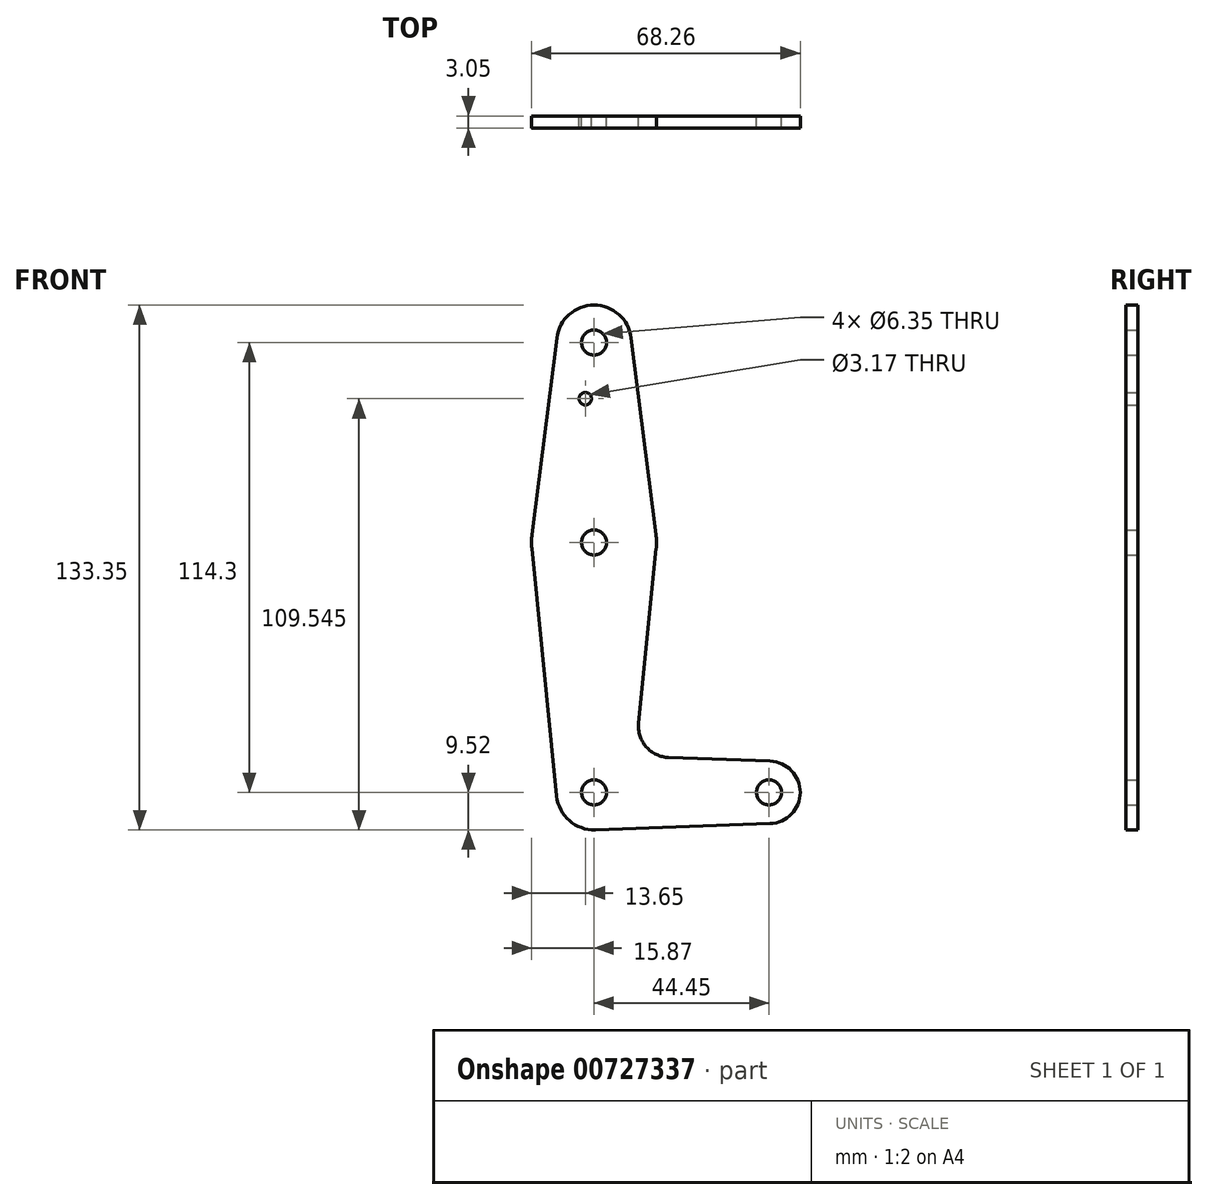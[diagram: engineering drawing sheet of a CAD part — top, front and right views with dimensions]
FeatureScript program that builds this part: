
annotation { "Feature Type Name" : "Feature", "Feature Type Description" : "" }
export const myFeature = defineFeature(function(context is Context, id is Id, definition is map)
    precondition{}
    {
        {
            var Q0;
            Q0=qCreatedBy(makeId("Front.planeOp"),FACE);
            var sketch = newSketch(context, id + "F0", { "sketchPlane" : qUnion([Q0])});
            skLineSegment(sketch, "E0", {"start": v(0, 0) * mm, "end": v(0, 114.3) * mm, "construction": true});
            skLineSegment(sketch, "E1", {"start": v(0, 0) * mm, "end": v(44.45, 0) * mm, "construction": true});
            skCircle(sketch, "E2", {"center": v(0, 114.3) * mm, "radius": 9.53 * mm});
            skCircle(sketch, "E3", {"center": v(0, 63.5) * mm, "radius": 15.88 * mm});
            skCircle(sketch, "E4", {"center": v(0, 0) * mm, "radius": 9.53 * mm});
            skCircle(sketch, "E5", {"center": v(44.45, 0) * mm, "radius": 7.94 * mm});
            skLineSegment(sketch, "E6", {"start": v(0, 63.5) * mm, "end": v(0, 0) * mm});
            skLineSegment(sketch, "E7", {"start": v(-9.45, 115.5) * mm, "end": v(-15.75, 65.48) * mm});
            skLineSegment(sketch, "E8", {"start": v(9.45, 115.5) * mm, "end": v(15.75, 65.48) * mm});
            skLineSegment(sketch, "E9", {"start": v(-15.8, 61.91) * mm, "end": v(-9.48, -0.95) * mm});
            skLineSegment(sketch, "E10", {"start": v(15.8, 61.91) * mm, "end": v(11.34, 17.6) * mm});
            skLineSegment(sketch, "E11", {"start": v(44.73, 7.93) * mm, "end": v(18.97, 8.85) * mm});
            skLineSegment(sketch, "E12", {"start": v(0.34, -9.52) * mm, "end": v(44.73, -7.93) * mm});
            skCircle(sketch, "E13", {"center": v(0, 114.3) * mm, "radius": 3.18 * mm});
            skCircle(sketch, "E14", {"center": v(0, 63.5) * mm, "radius": 3.18 * mm});
            skCircle(sketch, "E15", {"center": v(0, 0) * mm, "radius": 3.18 * mm});
            skCircle(sketch, "E16", {"center": v(44.45, 0) * mm, "radius": 3.18 * mm});
            skArc(sketch, "E17.filletArc", {"start": v(11.34, 17.6) * mm, "mid": v(13.26, 11.57) * mm, "end": v(18.97, 8.85) * mm});
            skCircle(sketch, "E18", {"center": v(-2.22, 100.03) * mm, "radius": 1.59 * mm});
            skLineSegment(sketch, "E19", {"start": v(0, 63.5) * mm, "end": v(0, 100.03) * mm});
            skSolve(sketch);
        }
        {
            var Q0;
            Q0 = qSketchRegion(id + "F0", true);
            extrude(context, id + "F1", {"entities" : qUnion([Q0]), "depth" : 3.05 * mm, "offsetDistance" : 25.4 * mm});
        }
    });
